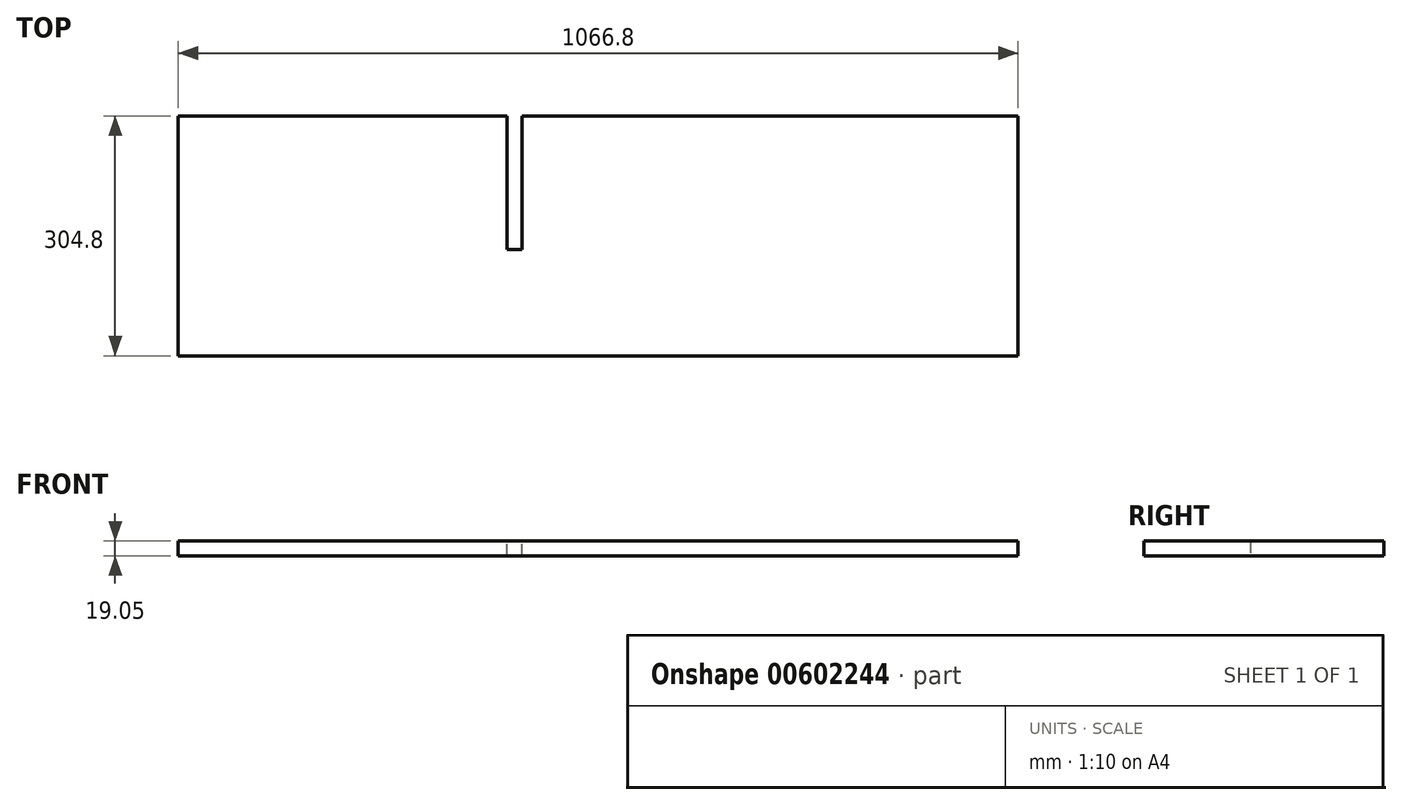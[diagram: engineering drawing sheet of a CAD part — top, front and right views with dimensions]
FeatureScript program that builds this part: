
annotation { "Feature Type Name" : "Feature", "Feature Type Description" : "" }
export const myFeature = defineFeature(function(context is Context, id is Id, definition is map)
    precondition{}
    {
        {
            var Q0;
            Q0=qCreatedBy(makeId("Top.planeOp"),FACE);
            var sketch = newSketch(context, id + "F0", { "sketchPlane" : qUnion([Q0])});
            skLineSegment(sketch, "E0.bottom", {"start": v(630.39, -135.23) * mm, "end": v(-436.41, -135.23) * mm});
            skLineSegment(sketch, "E0.top", {"start": v(630.39, 169.57) * mm, "end": v(-436.41, 169.57) * mm});
            skLineSegment(sketch, "E0.left", {"start": v(630.39, -135.23) * mm, "end": v(630.39, 169.57) * mm});
            skLineSegment(sketch, "E0.right", {"start": v(-436.41, -135.23) * mm, "end": v(-436.41, 169.57) * mm});
            skPoint(sketch, "E0.middle", {"position": v(96.99, 17.17) * mm});
            skSolve(sketch);
        }
        {
            var Q0;
            Q0=makeQuery(id+"F0.imprint","IMPRINT",FACE,{"disambiguationData":[TD([[makeQuery(id+"F0.imprint","IMPRINT",EDGE,{"derivedFrom":sQuery(id+"F0.wireOp",EDGE,"E0.bottom")}),-1.0]])]});
            extrude(context, id + "F1", {"entities" : qUnion([Q0]), "depth" : 19.05 * mm, "offsetDistance" : 25.4 * mm});
        }
        {
            var Q0;
            Q0=qCreatedBy(makeId("Right.planeOp"),FACE);
            var sketch = newSketch(context, id + "F2", { "sketchPlane" : qUnion([Q0])});
            skLineSegment(sketch, "E1.bottom", {"start": v(0, 129.9) * mm, "end": v(238.63, 129.9) * mm});
            skLineSegment(sketch, "E1.top", {"start": v(0, -100.87) * mm, "end": v(238.63, -100.87) * mm});
            skLineSegment(sketch, "E1.left", {"start": v(0, 129.9) * mm, "end": v(0, -100.87) * mm});
            skLineSegment(sketch, "E1.right", {"start": v(238.63, 129.9) * mm, "end": v(238.63, -100.87) * mm});
            skSolve(sketch);
        }
        {
            var Q0;
            Q0 = qSketchRegion(id + "F2", true);
            extrude(context, id + "F3", {"entities" : qUnion([Q0]), "operationType" : NewBodyOperationType.REMOVE, "oppositeDirection" : true, "depth" : 19.05 * mm, "offsetDistance" : 25.4 * mm});
        }
    });
